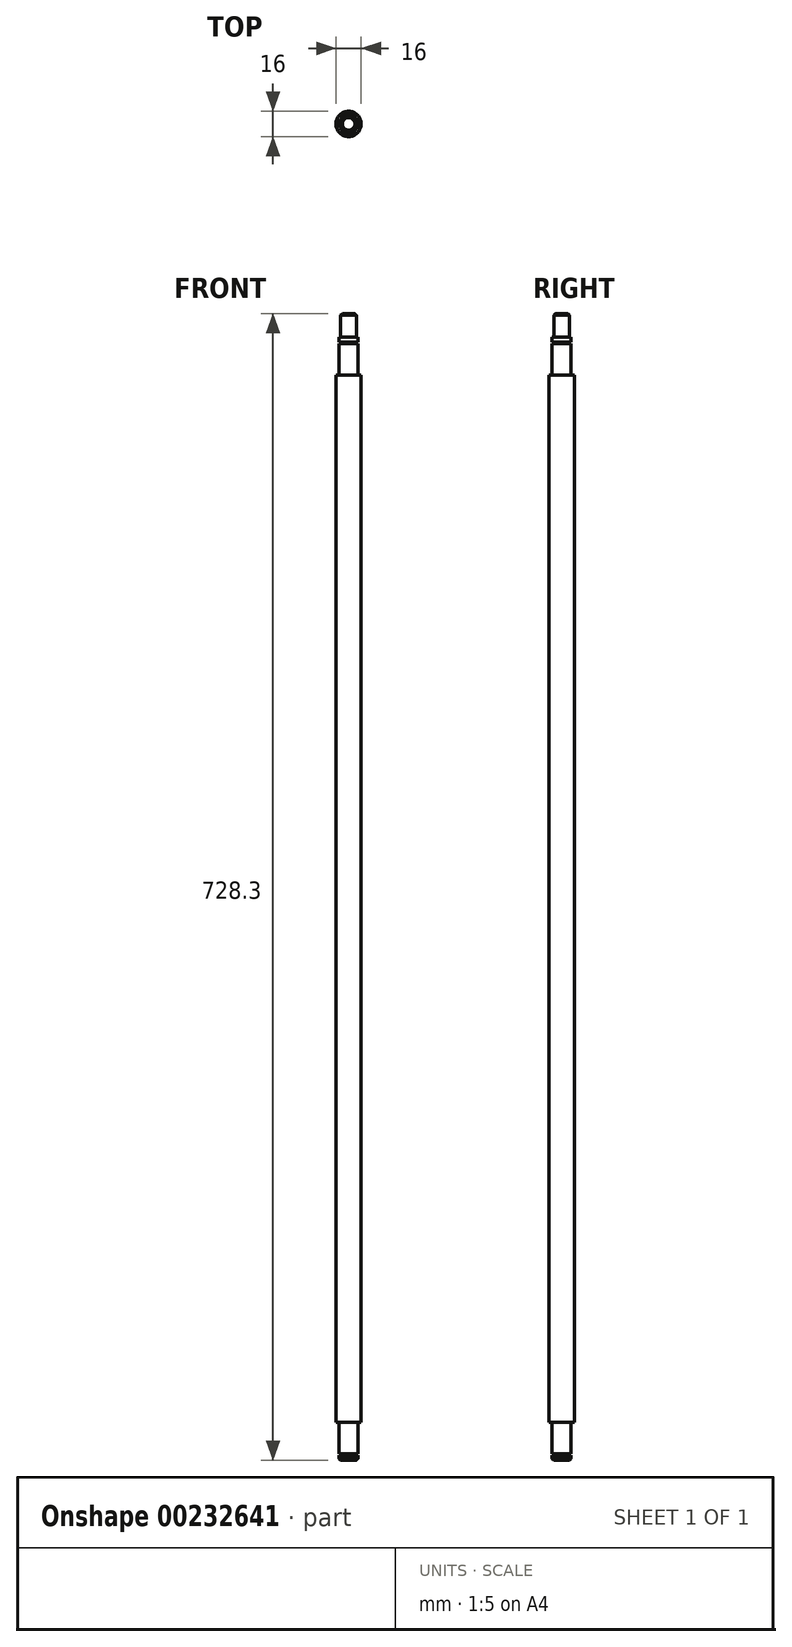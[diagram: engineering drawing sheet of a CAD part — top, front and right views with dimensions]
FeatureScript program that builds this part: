
annotation { "Feature Type Name" : "Feature", "Feature Type Description" : "" }
export const myFeature = defineFeature(function(context is Context, id is Id, definition is map)
    precondition{}
    {
        {
            var Q0;
            Q0=qCreatedBy(makeId("Top.planeOp"),FACE);
            var sketch = newSketch(context, id + "F0", { "sketchPlane" : qUnion([Q0])});
            skCircle(sketch, "E0", {"center": v(0, 0) * mm, "radius": 6 * mm});
            skSolve(sketch);
        }
        {
            var Q0;
            Q0=makeQuery(id+"F0.imprint","IMPRINT",FACE,{"disambiguationData":[TD([[makeQuery(id+"F0.imprint","IMPRINT",EDGE,{"derivedFrom":sQuery(id+"F0.wireOp",EDGE,"E0")}),1.0]])]});
            extrude(context, id + "F1", {"entities" : qUnion([Q0]), "depth" : 3 * mm});
        }
        {
            var Q0;
            Q0=makeQuery(id+"F1.opExtrude","CAP_FACE",FACE,{"disambiguationData":[OSD([sQuery(id+"F0.wireOp",EDGE,"E0")])],"isStart":false});
            var sketch = newSketch(context, id + "F2", { "sketchPlane" : qUnion([Q0])});
            skCircle(sketch, "E1", {"center": v(0, 0) * mm, "radius": 4.8 * mm});
            skSolve(sketch);
        }
        {
            var Q0;
            Q0=makeQuery(id+"F2.imprint","IMPRINT",FACE,{"disambiguationData":[TD([[makeQuery(id+"F2.imprint","IMPRINT",EDGE,{"derivedFrom":sQuery(id+"F2.wireOp",EDGE,"E1")}),1.0]])]});
            extrude(context, id + "F3", {"entities" : qUnion([Q0]), "operationType" : NewBodyOperationType.ADD, "depth" : 1.15 * mm});
        }
        {
            var Q0;
            Q0=makeQuery(id+"F3.opExtrude","CAP_FACE",FACE,{"disambiguationData":[OSD([sQuery(id+"F2.wireOp",EDGE,"E1")])],"isStart":false});
            var sketch = newSketch(context, id + "F4", { "sketchPlane" : qUnion([Q0])});
            skCircle(sketch, "E2", {"center": v(0, 0) * mm, "radius": 6 * mm});
            skSolve(sketch);
        }
        {
            var Q0;
            Q0=makeQuery(id+"F4.imprint","IMPRINT",FACE,{"disambiguationData":[TD([[makeQuery(id+"F4.imprint","IMPRINT",EDGE,{"derivedFrom":sQuery(id+"F4.wireOp",EDGE,"E2")}),1.0]])]});
            var Q1;
            Q1=makeQuery(id+"F4.imprint","IMPRINT",FACE,{"disambiguationData":[TD([[makeQuery(id+"F4.imprint","IMPRINT",EDGE,{"derivedFrom":makeQuery(id+"F3.opExtrude","CAP_EDGE",EDGE,{"disambiguationData":[OSD([sQuery(id+"F2.wireOp",EDGE,"E1")])],"isStart":false})}),1.0]])]});
            extrude(context, id + "F5", {"entities" : qUnion([Q0, Q1]), "operationType" : NewBodyOperationType.ADD, "depth" : 20 * mm});
        }
        {
            var Q0;
            Q0=makeQuery(id+"F5.opExtrude","CAP_FACE",FACE,{"disambiguationData":[OSD([sQuery(id+"F4.wireOp",EDGE,"E2")])],"isStart":false});
            var sketch = newSketch(context, id + "F6", { "sketchPlane" : qUnion([Q0])});
            skCircle(sketch, "E3", {"center": v(0, 0) * mm, "radius": 8 * mm});
            skSolve(sketch);
        }
        {
            var Q0;
            Q0=makeQuery(id+"F6.imprint","IMPRINT",FACE,{"disambiguationData":[TD([[makeQuery(id+"F6.imprint","IMPRINT",EDGE,{"derivedFrom":makeQuery(id+"F5.opExtrude","CAP_EDGE",EDGE,{"disambiguationData":[OSD([sQuery(id+"F4.wireOp",EDGE,"E2")])],"isStart":false})}),1.0]])]});
            var Q1;
            Q1=makeQuery(id+"F6.imprint","IMPRINT",FACE,{"disambiguationData":[TD([[makeQuery(id+"F6.imprint","IMPRINT",EDGE,{"derivedFrom":sQuery(id+"F6.wireOp",EDGE,"E3")}),1.0]])]});
            extrude(context, id + "F7", {"entities" : qUnion([Q0, Q1]), "operationType" : NewBodyOperationType.ADD, "depth" : 665 * mm});
        }
        {
            var Q0;
            Q0=makeQuery(id+"F7.opExtrude","CAP_FACE",FACE,{"disambiguationData":[OSD([sQuery(id+"F6.wireOp",EDGE,"E3")])],"isStart":false});
            var sketch = newSketch(context, id + "F8", { "sketchPlane" : qUnion([Q0])});
            skCircle(sketch, "E4", {"center": v(0, 0) * mm, "radius": 6 * mm});
            skSolve(sketch);
        }
        {
            var Q0;
            Q0=makeQuery(id+"F8.imprint","IMPRINT",FACE,{"disambiguationData":[TD([[makeQuery(id+"F8.imprint","IMPRINT",EDGE,{"derivedFrom":sQuery(id+"F8.wireOp",EDGE,"E4")}),1.0]])]});
            extrude(context, id + "F9", {"entities" : qUnion([Q0]), "operationType" : NewBodyOperationType.ADD, "depth" : 20 * mm});
        }
        {
            var Q0;
            Q0=makeQuery(id+"F9.opExtrude","CAP_FACE",FACE,{"disambiguationData":[OSD([sQuery(id+"F8.wireOp",EDGE,"E4")])],"isStart":false});
            var sketch = newSketch(context, id + "F10", { "sketchPlane" : qUnion([Q0])});
            skCircle(sketch, "E5", {"center": v(0, 0) * mm, "radius": 4.8 * mm});
            skSolve(sketch);
        }
        {
            var Q0;
            Q0=makeQuery(id+"F10.imprint","IMPRINT",FACE,{"disambiguationData":[TD([[makeQuery(id+"F10.imprint","IMPRINT",EDGE,{"derivedFrom":sQuery(id+"F10.wireOp",EDGE,"E5")}),1.0]])]});
            extrude(context, id + "F11", {"entities" : qUnion([Q0]), "operationType" : NewBodyOperationType.ADD, "depth" : 1.15 * mm});
        }
        {
            var Q0;
            Q0=makeQuery(id+"F11.opExtrude","CAP_FACE",FACE,{"disambiguationData":[OSD([sQuery(id+"F10.wireOp",EDGE,"E5")])],"isStart":false});
            var sketch = newSketch(context, id + "F12", { "sketchPlane" : qUnion([Q0])});
            skCircle(sketch, "E6", {"center": v(0, 0) * mm, "radius": 6 * mm});
            skSolve(sketch);
        }
        {
            var Q0;
            Q0=makeQuery(id+"F12.imprint","IMPRINT",FACE,{"disambiguationData":[TD([[makeQuery(id+"F12.imprint","IMPRINT",EDGE,{"derivedFrom":makeQuery(id+"F11.opExtrude","CAP_EDGE",EDGE,{"disambiguationData":[OSD([sQuery(id+"F10.wireOp",EDGE,"E5")])],"isStart":false})}),1.0]])]});
            var Q1;
            Q1=makeQuery(id+"F12.imprint","IMPRINT",FACE,{"disambiguationData":[TD([[makeQuery(id+"F12.imprint","IMPRINT",EDGE,{"derivedFrom":sQuery(id+"F12.wireOp",EDGE,"E6")}),1.0]])]});
            extrude(context, id + "F13", {"entities" : qUnion([Q0, Q1]), "operationType" : NewBodyOperationType.ADD, "depth" : 3 * mm});
        }
        {
            var Q0;
            Q0=makeQuery(id+"F13.opExtrude","CAP_FACE",FACE,{"disambiguationData":[OSD([sQuery(id+"F12.wireOp",EDGE,"E6")])],"isStart":false});
            var sketch = newSketch(context, id + "F14", { "sketchPlane" : qUnion([Q0])});
            skCircle(sketch, "E7", {"center": v(0, 0) * mm, "radius": 5 * mm});
            skSolve(sketch);
        }
        {
            var Q0;
            Q0=makeQuery(id+"F14.imprint","IMPRINT",FACE,{"disambiguationData":[TD([[makeQuery(id+"F14.imprint","IMPRINT",EDGE,{"derivedFrom":sQuery(id+"F14.wireOp",EDGE,"E7")}),1.0]])]});
            extrude(context, id + "F15", {"entities" : qUnion([Q0]), "operationType" : NewBodyOperationType.ADD, "depth" : 15 * mm});
        }
        {
            var Q0;
            Q0=makeQuery(id+"F15.opExtrude","CAP_EDGE",EDGE,{"disambiguationData":[OSD([sQuery(id+"F14.wireOp",EDGE,"E7")])],"isStart":false});
            var Q1;
            Q1=makeQuery(id+"F1.opExtrude","CAP_EDGE",EDGE,{"disambiguationData":[OSD([sQuery(id+"F0.wireOp",EDGE,"E0")])],"isStart":true});
            chamfer(context, id + "F16", {"entities" : qUnion([Q0, Q1]), "width" : 1 * mm, "tangentPropagation" : true});
        }
    });
